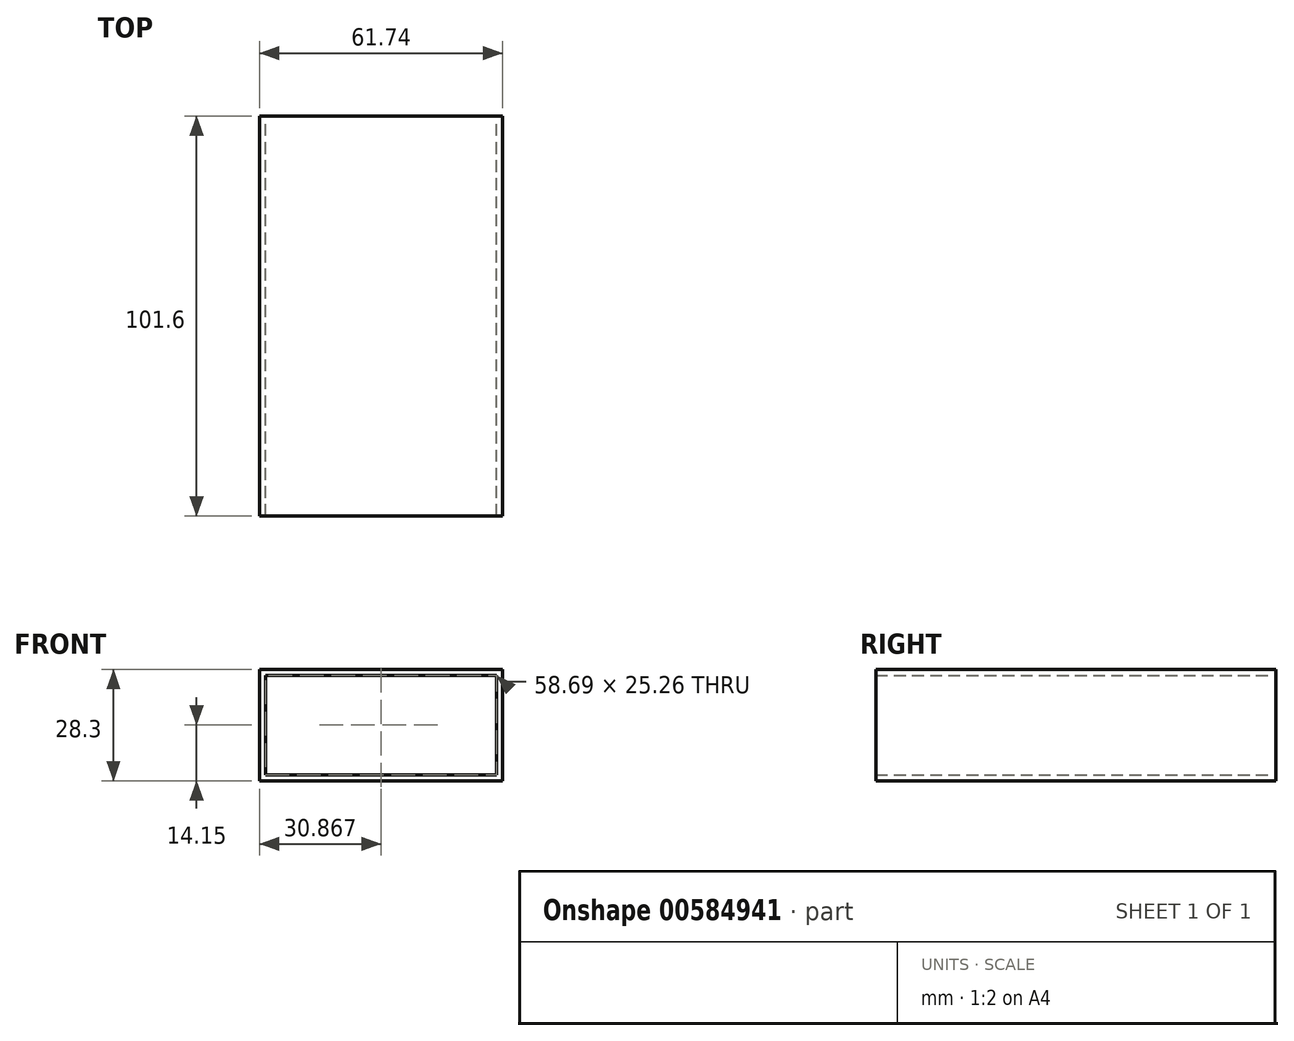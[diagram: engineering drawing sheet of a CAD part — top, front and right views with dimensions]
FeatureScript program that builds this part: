
annotation { "Feature Type Name" : "Feature", "Feature Type Description" : "" }
export const myFeature = defineFeature(function(context is Context, id is Id, definition is map)
    precondition{}
    {
        {
            var Q0;
            Q0=qCreatedBy(makeId("Front.planeOp"),FACE);
            var sketch = newSketch(context, id + "F0", { "sketchPlane" : qUnion([Q0])});
            skLineSegment(sketch, "E0.bottom", {"start": v(-53.57, 47) * mm, "end": v(8.17, 47) * mm});
            skLineSegment(sketch, "E0.top", {"start": v(-53.57, 18.7) * mm, "end": v(8.17, 18.7) * mm});
            skLineSegment(sketch, "E0.left", {"start": v(-53.57, 47) * mm, "end": v(-53.57, 18.7) * mm});
            skLineSegment(sketch, "E0.right", {"start": v(8.17, 47) * mm, "end": v(8.17, 18.7) * mm});
            skLineSegment(sketch, "E1.0", {"start": v(-52.05, 45.48) * mm, "end": v(6.64, 45.48) * mm});
            skLineSegment(sketch, "E1.1", {"start": v(-52.05, 45.48) * mm, "end": v(-52.05, 20.22) * mm});
            skLineSegment(sketch, "E1.2", {"start": v(-52.05, 20.22) * mm, "end": v(6.64, 20.22) * mm});
            skLineSegment(sketch, "E1.3", {"start": v(6.64, 45.48) * mm, "end": v(6.64, 20.22) * mm});
            skSolve(sketch);
        }
        {
            var Q0;
            Q0=makeQuery(id+"F0.imprint","IMPRINT",FACE,{"disambiguationData":[TD([[makeQuery(id+"F0.imprint","IMPRINT",EDGE,{"derivedFrom":sQuery(id+"F0.wireOp",EDGE,"E0.bottom")}),-1.0]])]});
            extrude(context, id + "F1", {"entities" : qUnion([Q0]), "depth" : 101.6 * mm, "offsetDistance" : 25.4 * mm});
        }
    });
